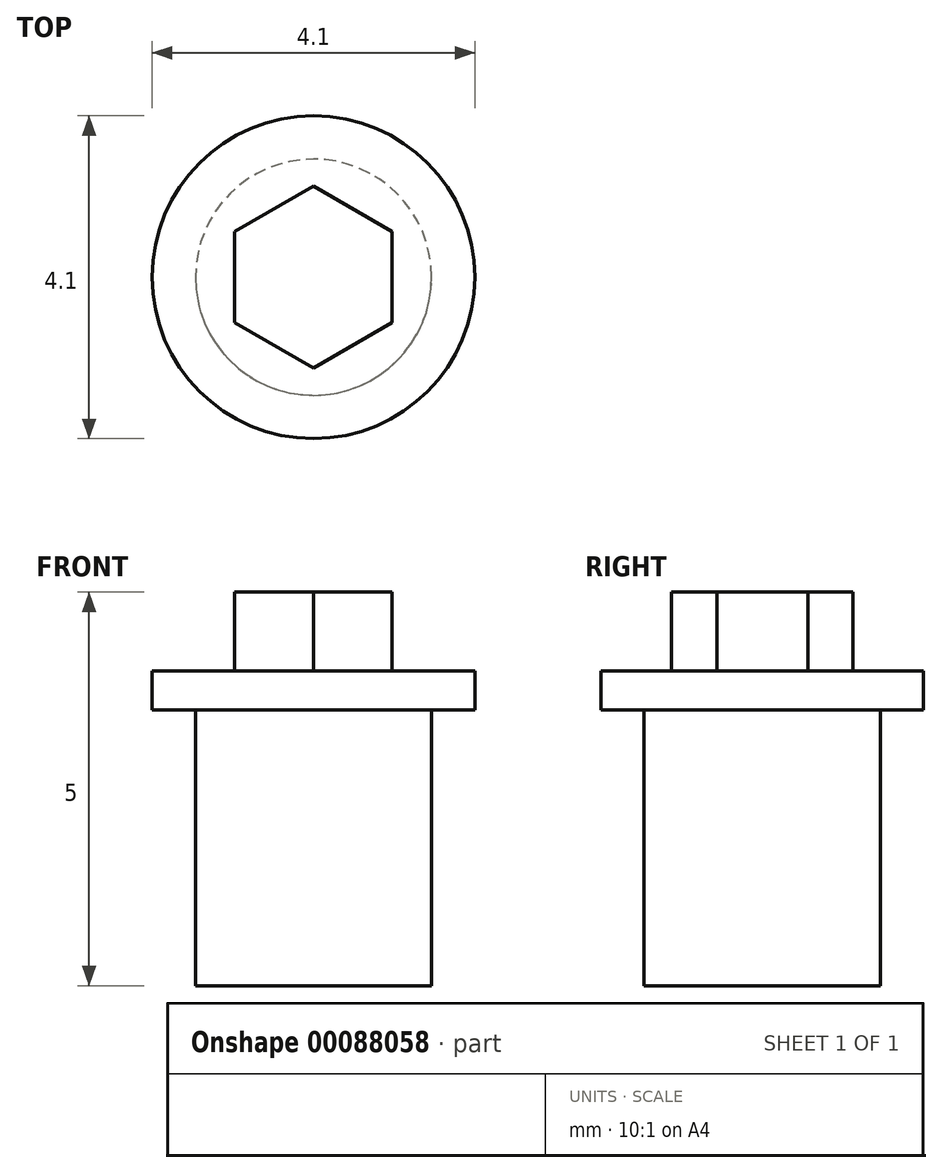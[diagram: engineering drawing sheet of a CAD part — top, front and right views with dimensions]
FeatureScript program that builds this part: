
annotation { "Feature Type Name" : "Feature", "Feature Type Description" : "" }
export const myFeature = defineFeature(function(context is Context, id is Id, definition is map)
    precondition{}
    {
        {
            var Q0;
            Q0=qCreatedBy(makeId("Top.planeOp"),FACE);
            var sketch = newSketch(context, id + "F0", { "sketchPlane" : qUnion([Q0])});
            skLineSegment(sketch, "E0", {"start": v(-1, 0) * mm, "end": v(1, 0) * mm});
            skLineSegment(sketch, "E1", {"start": v(-1, 0.58) * mm, "end": v(-1, -0.58) * mm});
            skLineSegment(sketch, "E2", {"start": v(1, 0.58) * mm, "end": v(1, -0.58) * mm});
            skLineSegment(sketch, "E3", {"start": v(-1, 0.58) * mm, "end": v(0, 1.15) * mm});
            skLineSegment(sketch, "E4", {"start": v(0, 1.15) * mm, "end": v(1, 0.58) * mm});
            skLineSegment(sketch, "E5", {"start": v(-1, -0.58) * mm, "end": v(0, -1.15) * mm});
            skLineSegment(sketch, "E6", {"start": v(0, -1.15) * mm, "end": v(1, -0.58) * mm});
            skSolve(sketch);
        }
        {
            var Q0;
            Q0 = qSketchRegion(id + "F0", true);
            extrude(context, id + "F1", {"entities" : qUnion([Q0]), "depth" : 1 * mm, "offsetDistance" : 25 * mm});
        }
        {
            var Q0;
            Q0=makeQuery(id+"F1.opExtrude","CAP_FACE",FACE,{"disambiguationData":[OSD([sQuery(id+"F0.wireOp",EDGE,"E1"),sQuery(id+"F0.wireOp",EDGE,"E2"),sQuery(id+"F0.wireOp",EDGE,"E3"),sQuery(id+"F0.wireOp",EDGE,"E4"),sQuery(id+"F0.wireOp",EDGE,"E5"),sQuery(id+"F0.wireOp",EDGE,"E6")])],"isStart":true});
            var sketch = newSketch(context, id + "F2", { "sketchPlane" : qUnion([Q0])});
            skCircle(sketch, "E7", {"center": v(0, 0) * mm, "radius": 2.05 * mm});
            skSolve(sketch);
        }
        {
            var Q0;
            Q0 = qSketchRegion(id + "F2", true);
            extrude(context, id + "F3", {"entities" : qUnion([Q0]), "operationType" : NewBodyOperationType.ADD, "depth" : .5 * mm, "offsetDistance" : 25 * mm});
        }
        {
            var Q0;
            Q0=qCreatedBy(makeId("Top.planeOp"),FACE);
            var sketch = newSketch(context, id + "F4", { "sketchPlane" : qUnion([Q0])});
            skCircle(sketch, "E8", {"center": v(0, 0) * mm, "radius": 1.5 * mm});
            skSolve(sketch);
        }
        {
            var Q0;
            Q0 = qSketchRegion(id + "F4", true);
            extrude(context, id + "F5", {"entities" : qUnion([Q0]), "operationType" : NewBodyOperationType.ADD, "oppositeDirection" : true, "depth" : 4 * mm, "offsetDistance" : 25 * mm});
        }
    });
